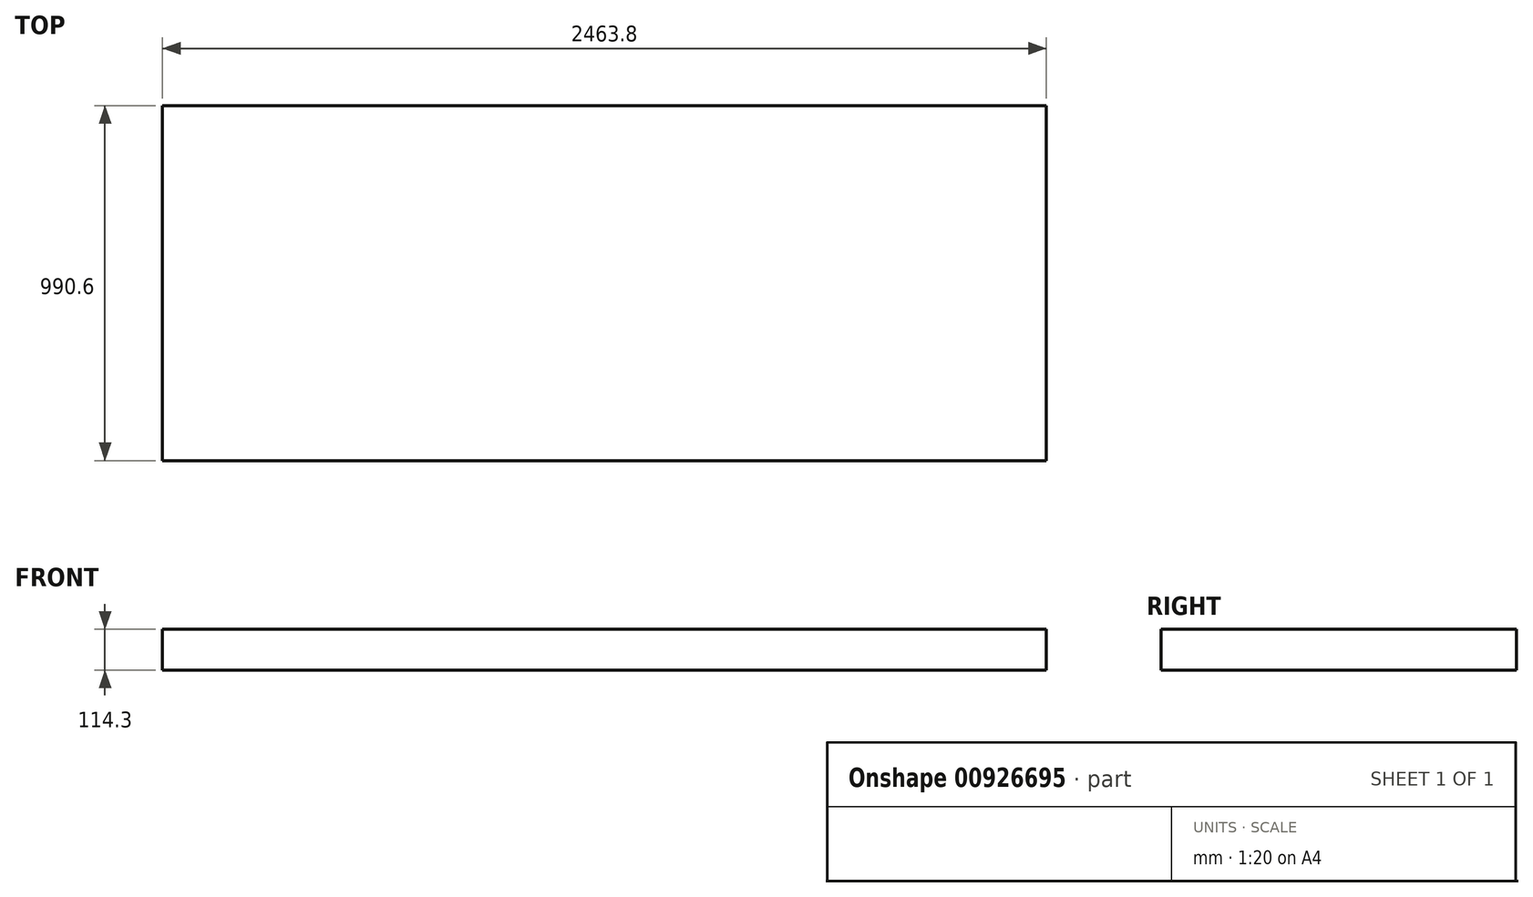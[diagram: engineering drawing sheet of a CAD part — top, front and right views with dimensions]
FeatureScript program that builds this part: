
annotation { "Feature Type Name" : "Feature", "Feature Type Description" : "" }
export const myFeature = defineFeature(function(context is Context, id is Id, definition is map)
    precondition{}
    {
        {
            var Q0;
            Q0=qCreatedBy(makeId("Top.planeOp"),FACE);
            var sketch = newSketch(context, id + "F0", { "sketchPlane" : qUnion([Q0])});
            skLineSegment(sketch, "E0.bottom", {"start": v(0, 0) * mm, "end": v(2463.8, 0) * mm});
            skLineSegment(sketch, "E0.top", {"start": v(0, 990.6) * mm, "end": v(2463.8, 990.6) * mm});
            skLineSegment(sketch, "E0.left", {"start": v(0, 0) * mm, "end": v(0, 990.6) * mm});
            skLineSegment(sketch, "E0.right", {"start": v(2463.8, 0) * mm, "end": v(2463.8, 990.6) * mm});
            skSolve(sketch);
        }
        {
            var Q0;
            Q0 = qSketchRegion(id + "F0", true);
            extrude(context, id + "F1", {"entities" : qUnion([Q0]), "depth" : -114.3 * mm, "offsetDistance" : 25.4 * mm});
        }
    });
